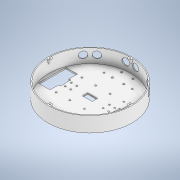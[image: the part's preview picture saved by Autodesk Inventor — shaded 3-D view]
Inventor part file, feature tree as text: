
AUTODESK INVENTOR PART (.ipt)
format: ipt  version: 2021 (Build 250183000, 183)  size: 446,464 bytes
history: native  units: mm
features: extrude x12, other x9, sketch x8, plane x8, reference x6, pattern_circular x2, hole x2, mirror x1, loft x1, projected_geometry x1
ambient origin geometry x8: Origin, YZ Plane, XZ Plane, XY Plane, X Axis, Y Axis, Z Axis, Center Point
bodies: Volumenkörper1 (feature_tree)
feature tree (50):
  other  "00_Mastersketch.ipt"
  extrude  "Extrusion1"  Depth=3.6mm TaperAngle=0.0deg
  extrude  "Extrusion2"  Depth=36.0mm
  extrude  "Extrusion3"  Depth=45.0mm
  extrude  "Extrusion5"  Depth=4.0mm
  pattern_circular  "Runde Anordnung1"  Count=64 Angle=360.0deg
  extrude  "Extrusion4"  TaperAngle=0.0deg  [1 undecoded]
  extrude  "Extrusion8"  TaperAngle=0.0deg  [1 undecoded]
  mirror  "Spiegeln1"
  sketch  "Skizze3"  dims[d3=45.0mm d4=0.0mm d5=36.0mm]
  plane  "Arbeitsebene1"
  sketch  "Skizze4"  dims[d6=0.0mm d7=45.0mm]
  loft  "Erhebung2"
  hole  "Bohrung2"  [1 undecoded]
  pattern_circular  "Runde Anordnung2"  [2 undecoded]
  plane  "Arbeitsebene2"
  extrude  "Extrusion6"  Depth=10.0mm TaperAngle=0.0deg
  extrude  "Extrusion7"  Depth=10.0mm TaperAngle=0.0deg
  extrude  "Extrusion9"  TaperAngle=0.0deg  [1 undecoded]
  plane  "Arbeitsebene_Ultra_1_Extrusion"
  plane  "Arbeitsebene_Ultra_2_Extrusion"
  extrude  "Extrusion11"  Depth=2.0mm
  extrude  "Extrusion12"  TaperAngle=0.0deg  [1 undecoded]
  hole  "Bohrung3"  [1 undecoded]
  extrude  "Extrusion10"  TaperAngle=0.0deg  [1 undecoded]
  other  "01_caseBottom"
  sketch  "Skizze2"  dims[d0=10.0mm d1=3.6mm d2=0.0mm]
  other  "3D-Skizze2"
  other  "Arbeitsachse1"
  sketch  "Skizze5"  dims[d8=0.0mm d9=4.0mm]
  reference  "Referenz1"
  reference  "Referenz2"
  sketch  "Skizze6"  dims[d10=6.0mm]
  plane  "Arbeitsebene_Ultra_1_Angle"
  plane  "Arbeitsebene_Ultra_1_Extrusion_Helper"
  plane  "Arbeitsebene_Ultra_2_"
  plane  "Arbeitsebene_Ultra_2_Extrusion_Helper"
  sketch  "Skizze7"  dims[d11=0.0mm d12=0.0mm d13=640.0mm d14=360.0deg]
  projected_geometry  "Projizierte Kontur1"
  reference  "Referenz3"
  reference  "Referenz4"
  sketch  "Skizze8"  dims[d17=-15.0mm d31=0.0mm d32=90.0deg]
  reference  "Referenz5"
  reference  "Referenz6"
  sketch  "Skizze9"  dims[d33=0.0mm d34=90.0deg d35=0.0mm d36=90.0deg d37=3.35mm d38=6.0mm d39=4.0mm d40=2.0mm d41=90.0deg d42=5.0mm d43=0.0mm d44=40.0mm d45=360.0deg d47=1.0mm d48=1.0mm d49=10.0mm d50=0.0mm d51=10.0mm d52=0.0mm d53=0.0mm d54=0.0mm d55=2.0mm d56=0.0mm d57=0.0mm d58=1.0mm d60=0.0mm d61=0.0mm d62=45.0deg d63=90.0deg d64=-7.853982mm d65=90.0deg d66=1.0mm d67=10.0mm d68=0.0mm d69=1.0mm d70=10.0mm d71=0.0mm d74=4.2mm d75=0.2mm d76=110.0mm d77=40.0mm d78=36.0mm d79=4.0mm d80=6.0mm d81=4.0mm d82=2.0mm d83=90.0deg d84=5.0mm d85=0.0mm]
  other  "<userpath>\Desktop\Bachelorarbeit\CAD\00_RobotAssembly.iam"
  other  "00_RobotAssembly.iam"
  other  "HC-SR04:1"
  other  "HC-SR04:3"
  other  "HC-SR04:2"
note: 9 required parameter values undecoded (feature->parameter linkage not recoverable at this tier; creation-order binding heuristic only, values carry confidence <= 0.55)
